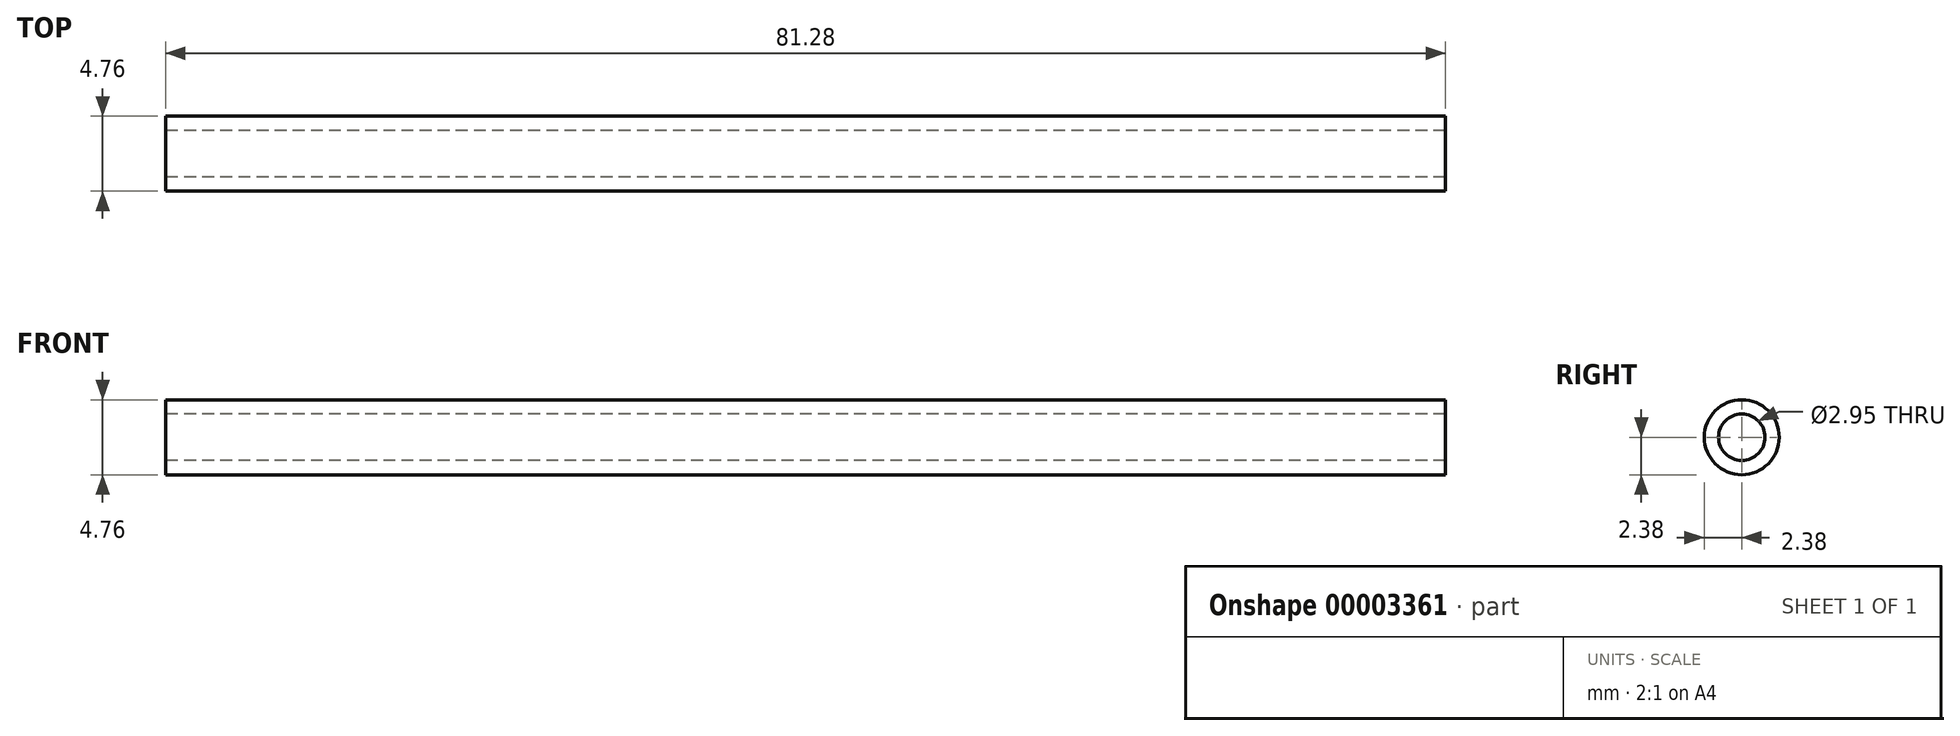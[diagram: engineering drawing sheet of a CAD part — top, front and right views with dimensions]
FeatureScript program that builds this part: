
annotation { "Feature Type Name" : "Feature", "Feature Type Description" : "" }
export const myFeature = defineFeature(function(context is Context, id is Id, definition is map)
    precondition{}
    {
        {
            var Q0;
            Q0=qCreatedBy(makeId("Right.planeOp"),FACE);
            var sketch = newSketch(context, id + "F0", { "sketchPlane" : qUnion([Q0])});
            skCircle(sketch, "E0", {"center": v(0, 0) * mm, "radius": 2.38 * mm});
            skCircle(sketch, "E1", {"center": v(0, 0) * mm, "radius": 1.47 * mm});
            skSolve(sketch);
        }
        {
            var Q0;
            Q0=qSketchRegion(id+"F0",true);
            extrude(context, id + "F1", {"entities" : qUnion([Q0]), "endBound" : BoundingType.SYMMETRIC, "depth" : 81.28 * mm});
        }
    });
